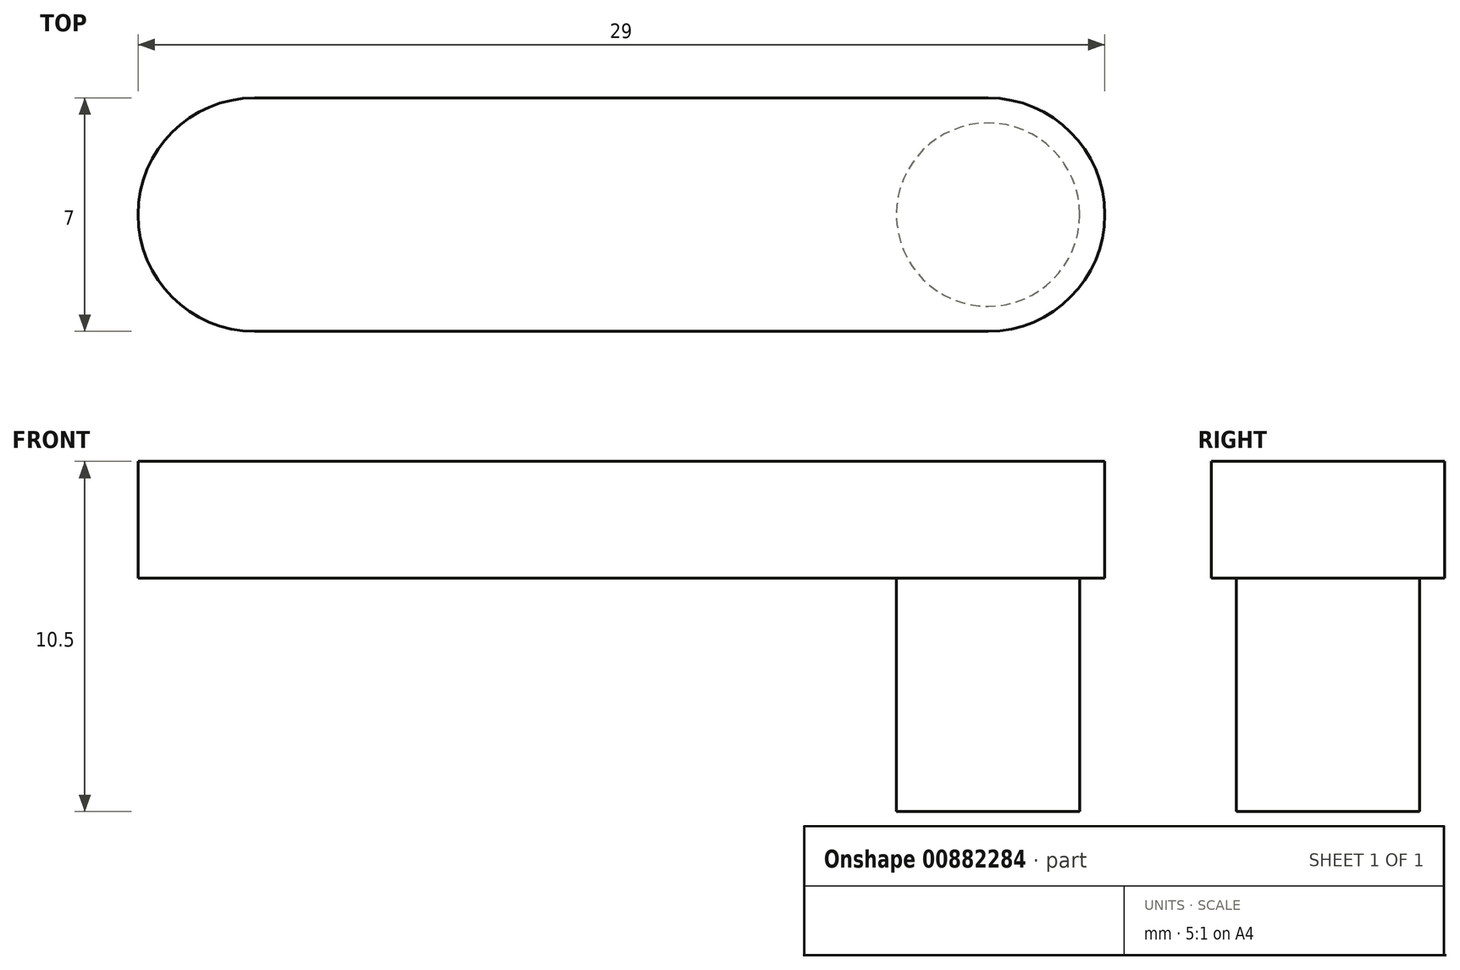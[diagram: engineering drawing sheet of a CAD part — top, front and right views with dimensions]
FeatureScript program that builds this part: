
annotation { "Feature Type Name" : "Feature", "Feature Type Description" : "" }
export const myFeature = defineFeature(function(context is Context, id is Id, definition is map)
    precondition{}
    {
        {
            var Q0;
            Q0=qCreatedBy(makeId("Top.planeOp"),FACE);
            var sketch = newSketch(context, id + "F0", { "sketchPlane" : qUnion([Q0])});
            skLineSegment(sketch, "E0.bottom", {"start": v(3.5, 0) * mm, "end": v(25.5, 0) * mm});
            skLineSegment(sketch, "E0.top", {"start": v(3.5, 7) * mm, "end": v(25.5, 7) * mm});
            skLineSegment(sketch, "E0.left", {"start": v(0, 3.5) * mm, "end": v(0, 3.5) * mm});
            skLineSegment(sketch, "E0.right", {"start": v(29, 3.5) * mm, "end": v(29, 3.5) * mm});
            skPoint(sketch, "E1.visualSharp", {"position": v(0, 7) * mm});
            skArc(sketch, "E1.filletArc", {"start": v(3.5, 7) * mm, "mid": v(1.03, 5.97) * mm, "end": v(0, 3.5) * mm});
            skPoint(sketch, "E2.visualSharp", {"position": v(0, 0) * mm});
            skArc(sketch, "E2.filletArc", {"start": v(0, 3.5) * mm, "mid": v(1.03, 1.03) * mm, "end": v(3.5, 0) * mm});
            skPoint(sketch, "E3.visualSharp", {"position": v(29, 7) * mm});
            skArc(sketch, "E3.filletArc", {"start": v(29, 3.5) * mm, "mid": v(27.97, 5.97) * mm, "end": v(25.5, 7) * mm});
            skPoint(sketch, "E4.visualSharp", {"position": v(29, 0) * mm});
            skArc(sketch, "E4.filletArc", {"start": v(25.5, 0) * mm, "mid": v(27.97, 1.03) * mm, "end": v(29, 3.5) * mm});
            skSolve(sketch);
        }
        {
            var Q0;
            Q0=makeQuery(id+"F0.imprint","IMPRINT",FACE,{"disambiguationData":[TD([[makeQuery(id+"F0.imprint","IMPRINT",EDGE,{"derivedFrom":sQuery(id+"F0.wireOp",EDGE,"E0.bottom")}),1.0]])]});
            extrude(context, id + "F1", {"entities" : qUnion([Q0]), "depth" : 3.5 * mm, "offsetDistance" : 25 * mm});
        }
        {
            var Q0;
            Q0=makeQuery(id+"F1.opExtrude","CAP_FACE",FACE,{"disambiguationData":[OSD([sQuery(id+"F0.wireOp",EDGE,"E0.bottom"),sQuery(id+"F0.wireOp",EDGE,"E0.top"),sQuery(id+"F0.wireOp",EDGE,"E1.filletArc"),sQuery(id+"F0.wireOp",EDGE,"E2.filletArc"),sQuery(id+"F0.wireOp",EDGE,"E3.filletArc"),sQuery(id+"F0.wireOp",EDGE,"E4.filletArc")])],"isStart":true});
            var sketch = newSketch(context, id + "F2", { "sketchPlane" : qUnion([Q0])});
            skPoint(sketch, "E5", {"position": v(25.5, -3.5) * mm});
            skCircle(sketch, "E6", {"center": v(25.5, -3.5) * mm, "radius": 2.75 * mm});
            skSolve(sketch);
        }
        {
            var Q0;
            Q0=makeQuery(id+"F2.imprint","IMPRINT",FACE,{"disambiguationData":[TD([[makeQuery(id+"F2.imprint","IMPRINT",EDGE,{"derivedFrom":sQuery(id+"F2.wireOp",EDGE,"E6")}),1.0]])]});
            extrude(context, id + "F3", {"entities" : qUnion([Q0]), "operationType" : NewBodyOperationType.ADD, "depth" : 7 * mm, "offsetDistance" : 25 * mm});
        }
    });
